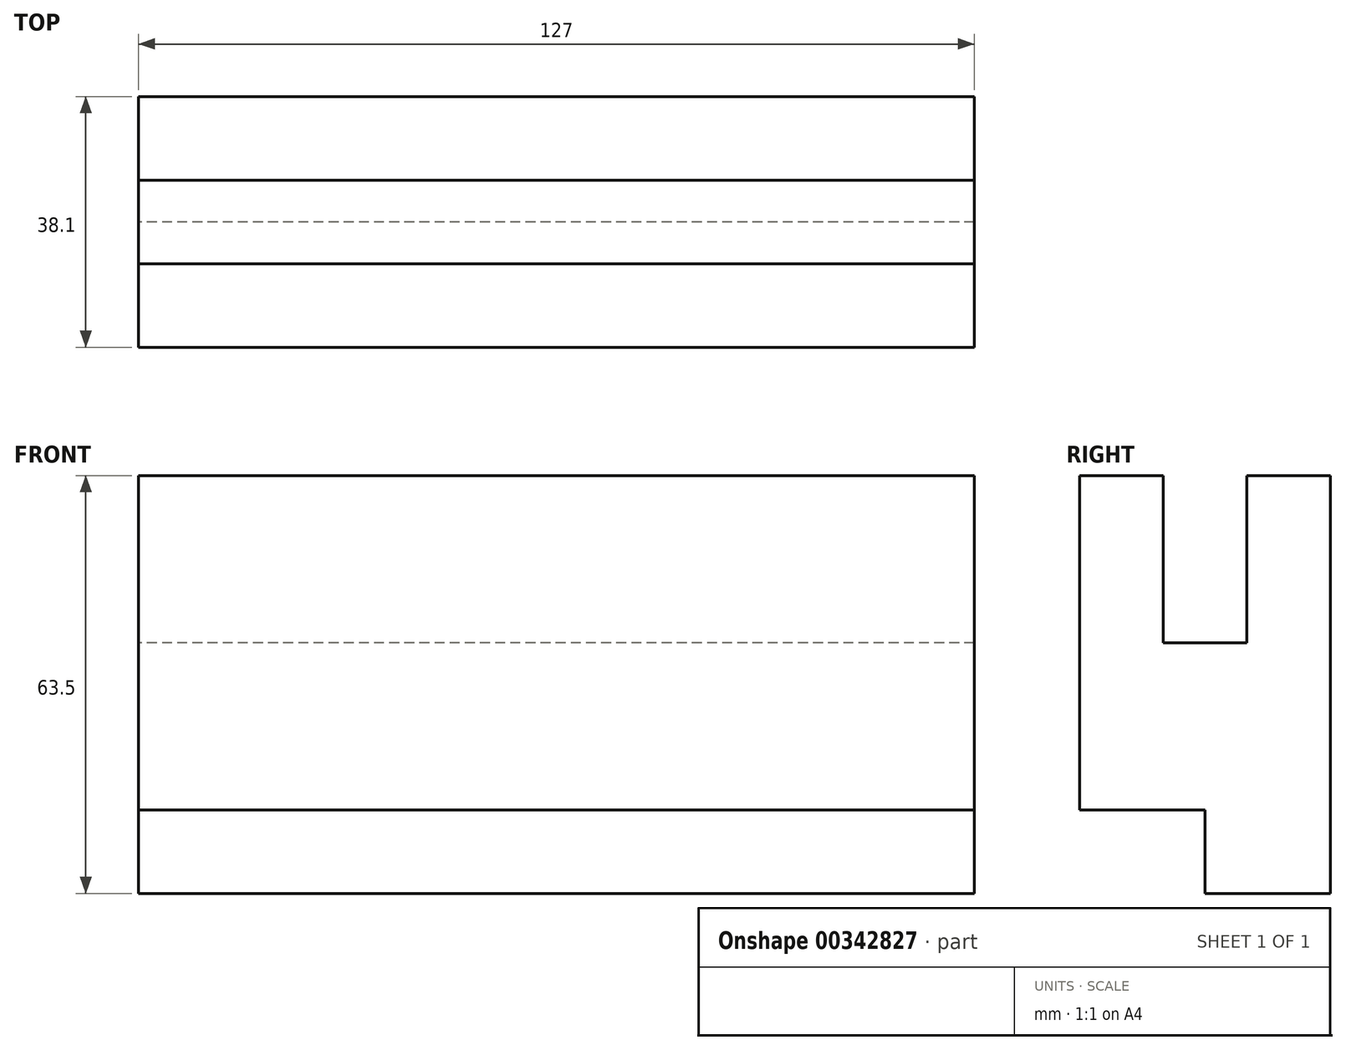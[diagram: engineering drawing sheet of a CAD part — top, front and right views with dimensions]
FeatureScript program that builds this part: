
annotation { "Feature Type Name" : "Feature", "Feature Type Description" : "" }
export const myFeature = defineFeature(function(context is Context, id is Id, definition is map)
    precondition{}
    {
        {
            var Q0;
            Q0=qCreatedBy(makeId("Right.planeOp"),FACE);
            var sketch = newSketch(context, id + "F0", { "sketchPlane" : qUnion([Q0])});
            skLineSegment(sketch, "E0", {"start": v(-26.53, 18.42) * mm, "end": v(-13.83, 18.42) * mm});
            skLineSegment(sketch, "E1", {"start": v(-26.53, 18.42) * mm, "end": v(-26.53, -32.38) * mm});
            skLineSegment(sketch, "E2", {"start": v(-26.53, -32.38) * mm, "end": v(-7.48, -32.38) * mm});
            skLineSegment(sketch, "E3", {"start": v(-7.48, -32.38) * mm, "end": v(-7.48, -45.08) * mm});
            skLineSegment(sketch, "E4", {"start": v(-7.48, -45.08) * mm, "end": v(11.57, -45.08) * mm});
            skLineSegment(sketch, "E5", {"start": v(11.57, -45.08) * mm, "end": v(11.57, 18.42) * mm});
            skLineSegment(sketch, "E6", {"start": v(11.57, 18.42) * mm, "end": v(-1.13, 18.42) * mm});
            skLineSegment(sketch, "E7", {"start": v(-1.13, 18.42) * mm, "end": v(-1.13, -6.98) * mm});
            skLineSegment(sketch, "E8", {"start": v(-1.13, -6.98) * mm, "end": v(-13.83, -6.98) * mm});
            skLineSegment(sketch, "E9", {"start": v(-13.83, -6.98) * mm, "end": v(-13.83, 18.42) * mm});
            skSolve(sketch);
        }
        {
            var Q0;
            Q0=makeQuery(id+"F0.imprint","IMPRINT",FACE,{"disambiguationData":[TD([[makeQuery(id+"F0.imprint","IMPRINT",EDGE,{"derivedFrom":sQuery(id+"F0.wireOp",EDGE,"E0")}),-1.0]])]});
            extrude(context, id + "F1", {"entities" : qUnion([Q0]), "depth" : 127 * mm});
        }
    });
